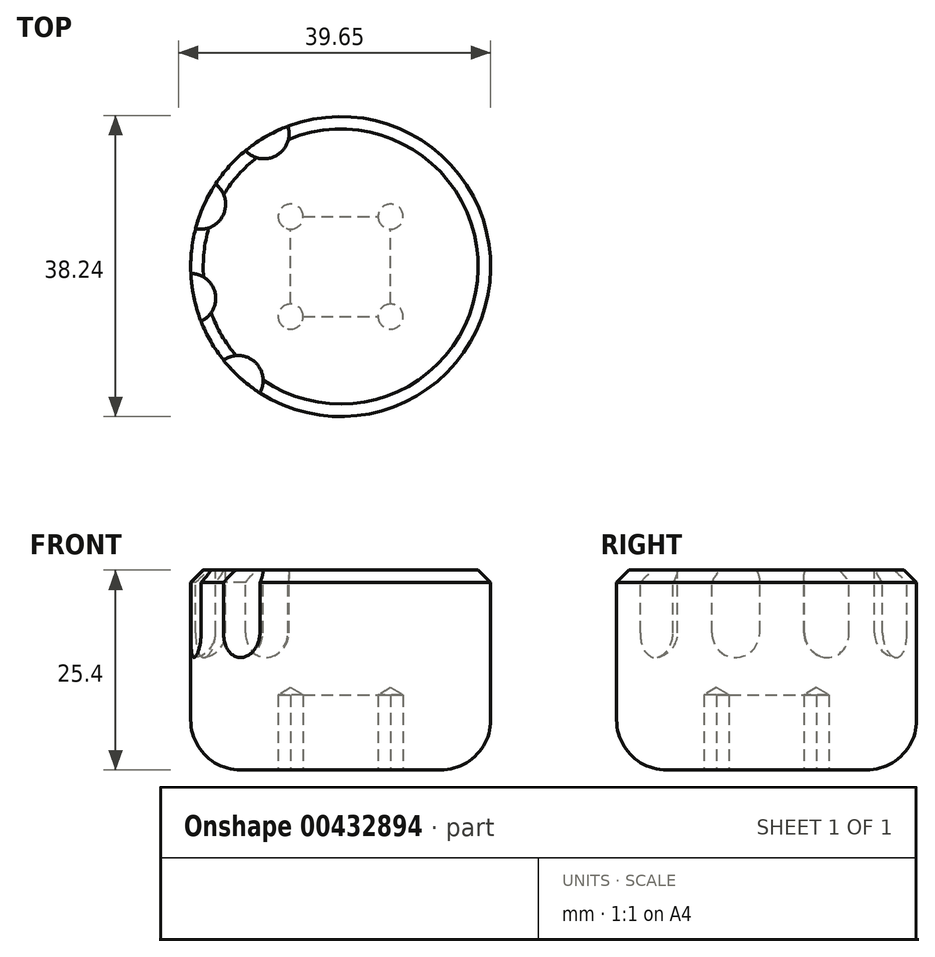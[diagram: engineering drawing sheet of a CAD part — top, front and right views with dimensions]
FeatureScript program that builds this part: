
annotation { "Feature Type Name" : "Feature", "Feature Type Description" : "" }
export const myFeature = defineFeature(function(context is Context, id is Id, definition is map)
    precondition{}
    {
        {
            var Q0;
            Q0=qCreatedBy(makeId("Top.planeOp"),FACE);
            var sketch = newSketch(context, id + "F0", { "sketchPlane" : qUnion([Q0])});
            skCircle(sketch, "E0", {"center": v(0, 0) * mm, "radius": 19.05 * mm});
            skSolve(sketch);
        }
        {
            var Q0;
            Q0 = qSketchRegion(id + "F0", true);
            extrude(context, id + "F1", {"entities" : qUnion([Q0]), "depth" : 25.4 * mm});
        }
        {
            var Q0;
            Q0=makeQuery(id+"F1.opExtrude","CAP_FACE",FACE,{"disambiguationData":[OSD([sQuery(id+"F0.wireOp",EDGE,"E0")])],"isStart":false});
            var sketch = newSketch(context, id + "F2", { "sketchPlane" : qUnion([Q0])});
            skCircle(sketch, "E1.cCircle", {"center": v(0, 0) * mm, "radius": 19.05 * mm, "construction": true});
            skLineSegment(sketch, "E1.0", {"start": v(-19.05, -4.05) * mm, "end": v(-19.05, 4.05) * mm});
            skLineSegment(sketch, "E1.1", {"start": v(-19.05, 4.05) * mm, "end": v(-15.76, 11.45) * mm});
            skLineSegment(sketch, "E1.2", {"start": v(-15.76, 11.45) * mm, "end": v(-9.74, 16.87) * mm});
            skLineSegment(sketch, "E1.3", {"start": v(-9.74, 16.87) * mm, "end": v(-2.04, 19.37) * mm});
            skLineSegment(sketch, "E1.4", {"start": v(-2.04, 19.37) * mm, "end": v(6.02, 18.52) * mm});
            skLineSegment(sketch, "E1.5", {"start": v(6.02, 18.52) * mm, "end": v(13.03, 14.47) * mm});
            skLineSegment(sketch, "E1.6", {"start": v(13.03, 14.47) * mm, "end": v(17.8, 7.92) * mm});
            skLineSegment(sketch, "E1.7", {"start": v(17.8, 7.92) * mm, "end": v(19.48, 0) * mm});
            skLineSegment(sketch, "E1.8", {"start": v(19.48, 0) * mm, "end": v(17.8, -7.92) * mm});
            skLineSegment(sketch, "E1.9", {"start": v(17.8, -7.92) * mm, "end": v(13.03, -14.47) * mm});
            skLineSegment(sketch, "E1.10", {"start": v(13.03, -14.47) * mm, "end": v(6.02, -18.52) * mm});
            skLineSegment(sketch, "E1.11", {"start": v(6.02, -18.52) * mm, "end": v(-2.04, -19.37) * mm});
            skLineSegment(sketch, "E1.12", {"start": v(-2.04, -19.37) * mm, "end": v(-9.74, -16.87) * mm});
            skLineSegment(sketch, "E1.13", {"start": v(-9.74, -16.87) * mm, "end": v(-15.76, -11.45) * mm});
            skLineSegment(sketch, "E1.14", {"start": v(-15.76, -11.45) * mm, "end": v(-19.05, -4.05) * mm});
            skPoint(sketch, "E1.0.midPoint", {"position": v(-19.05, 0) * mm});
            skCircle(sketch, "E2", {"center": v(-19.05, -4.05) * mm, "radius": 3.18 * mm});
            skCircle(sketch, "E3.1.0", {"center": v(-13.03, -14.47) * mm, "radius": 3.18 * mm});
            skCircle(sketch, "E3.2.0", {"center": v(-2.04, -19.37) * mm, "radius": 3.18 * mm});
            skCircle(sketch, "E3.3.0", {"center": v(9.74, -16.87) * mm, "radius": 3.18 * mm});
            skCircle(sketch, "E3.4.0", {"center": v(17.8, -7.92) * mm, "radius": 3.18 * mm});
            skCircle(sketch, "E3.5.0", {"center": v(19.05, 4.05) * mm, "radius": 3.18 * mm});
            skCircle(sketch, "E3.6.0", {"center": v(13.03, 14.47) * mm, "radius": 3.18 * mm});
            skCircle(sketch, "E3.7.0", {"center": v(2.04, 19.37) * mm, "radius": 3.18 * mm});
            skCircle(sketch, "E3.8.0", {"center": v(-9.74, 16.87) * mm, "radius": 3.18 * mm});
            skCircle(sketch, "E3.9.0", {"center": v(-17.8, 7.92) * mm, "radius": 3.18 * mm});
            skSolve(sketch);
        }
        {
            var Q0;
            {var subQ0=sQuery(id+"F2.wireOp",EDGE,"E3.9.0");var subQ1=makeQuery(id+"F1.opExtrude","CAP_EDGE",EDGE,{"disambiguationData":[OSD([sQuery(id+"F0.wireOp",EDGE,"E0")])],"isStart":false});var subQ2=makeQuery(id+"F2.imprint","INTERSECT",VERTEX,{"disambiguationData":[OD(0.0)],"derivedFrom":[subQ1,subQ0]});Q0=makeQuery(id+"F2.imprint","IMPRINT",FACE,{"disambiguationData":[TD([[makeQuery(id+"F2.imprint","IMPRINT",EDGE,{"disambiguationData":[TD([[subQ2,1.0]])],"derivedFrom":subQ0}),1.0]])]});}
            var Q1;
            {var subQ0=sQuery(id+"F2.wireOp",EDGE,"E2");var subQ1=makeQuery(id+"F1.opExtrude","CAP_EDGE",EDGE,{"disambiguationData":[OSD([sQuery(id+"F0.wireOp",EDGE,"E0")])],"isStart":false});var subQ2=makeQuery(id+"F2.imprint","INTERSECT",VERTEX,{"disambiguationData":[OD(0.0)],"derivedFrom":[subQ1,subQ0]});Q1=makeQuery(id+"F2.imprint","IMPRINT",FACE,{"disambiguationData":[TD([[makeQuery(id+"F2.imprint","IMPRINT",EDGE,{"disambiguationData":[TD([[subQ2,1.0]])],"derivedFrom":subQ0}),1.0]])]});}
            var Q2;
            {var subQ0=sQuery(id+"F2.wireOp",EDGE,"E3.1.0");var subQ1=makeQuery(id+"F1.opExtrude","CAP_EDGE",EDGE,{"disambiguationData":[OSD([sQuery(id+"F0.wireOp",EDGE,"E0")])],"isStart":false});var subQ2=makeQuery(id+"F2.imprint","INTERSECT",VERTEX,{"disambiguationData":[OD(0.0)],"derivedFrom":[subQ1,subQ0]});Q2=makeQuery(id+"F2.imprint","IMPRINT",FACE,{"disambiguationData":[TD([[makeQuery(id+"F2.imprint","IMPRINT",EDGE,{"disambiguationData":[TD([[subQ2,1.0]])],"derivedFrom":subQ0}),1.0]])]});}
            var Q3;
            {var subQ0=sQuery(id+"F2.wireOp",EDGE,"E3.2.0");var subQ1=makeQuery(id+"F1.opExtrude","CAP_EDGE",EDGE,{"disambiguationData":[OSD([sQuery(id+"F0.wireOp",EDGE,"E0")])],"isStart":false});var subQ2=makeQuery(id+"F2.imprint","INTERSECT",VERTEX,{"disambiguationData":[OD(0.0)],"derivedFrom":[subQ1,subQ0]});Q3=makeQuery(id+"F2.imprint","IMPRINT",FACE,{"disambiguationData":[TD([[makeQuery(id+"F2.imprint","IMPRINT",EDGE,{"disambiguationData":[TD([[subQ2,1.0]])],"derivedFrom":subQ0}),1.0]])]});}
            var Q4;
            {var subQ0=sQuery(id+"F2.wireOp",EDGE,"E3.3.0");var subQ1=makeQuery(id+"F1.opExtrude","CAP_EDGE",EDGE,{"disambiguationData":[OSD([sQuery(id+"F0.wireOp",EDGE,"E0")])],"isStart":false});var subQ2=makeQuery(id+"F2.imprint","INTERSECT",VERTEX,{"disambiguationData":[OD(0.0)],"derivedFrom":[subQ1,subQ0]});Q4=makeQuery(id+"F2.imprint","IMPRINT",FACE,{"disambiguationData":[TD([[makeQuery(id+"F2.imprint","IMPRINT",EDGE,{"disambiguationData":[TD([[subQ2,1.0]])],"derivedFrom":subQ0}),1.0]])]});}
            var Q5;
            {var subQ0=sQuery(id+"F2.wireOp",EDGE,"E3.4.0");var subQ1=makeQuery(id+"F1.opExtrude","CAP_EDGE",EDGE,{"disambiguationData":[OSD([sQuery(id+"F0.wireOp",EDGE,"E0")])],"isStart":false});var subQ2=makeQuery(id+"F2.imprint","INTERSECT",VERTEX,{"disambiguationData":[OD(0.0)],"derivedFrom":[subQ1,subQ0]});Q5=makeQuery(id+"F2.imprint","IMPRINT",FACE,{"disambiguationData":[TD([[makeQuery(id+"F2.imprint","IMPRINT",EDGE,{"disambiguationData":[TD([[subQ2,1.0]])],"derivedFrom":subQ0}),1.0]])]});}
            var Q6;
            {var subQ0=sQuery(id+"F2.wireOp",EDGE,"E3.5.0");var subQ1=makeQuery(id+"F1.opExtrude","CAP_EDGE",EDGE,{"disambiguationData":[OSD([sQuery(id+"F0.wireOp",EDGE,"E0")])],"isStart":false});var subQ2=makeQuery(id+"F2.imprint","INTERSECT",VERTEX,{"disambiguationData":[OD(0.0)],"derivedFrom":[subQ1,subQ0]});Q6=makeQuery(id+"F2.imprint","IMPRINT",FACE,{"disambiguationData":[TD([[makeQuery(id+"F2.imprint","IMPRINT",EDGE,{"disambiguationData":[TD([[subQ2,1.0]])],"derivedFrom":subQ0}),1.0]])]});}
            var Q7;
            {var subQ0=sQuery(id+"F2.wireOp",EDGE,"E3.6.0");var subQ1=makeQuery(id+"F1.opExtrude","CAP_EDGE",EDGE,{"disambiguationData":[OSD([sQuery(id+"F0.wireOp",EDGE,"E0")])],"isStart":false});var subQ2=makeQuery(id+"F2.imprint","INTERSECT",VERTEX,{"disambiguationData":[OD(0.0)],"derivedFrom":[subQ1,subQ0]});Q7=makeQuery(id+"F2.imprint","IMPRINT",FACE,{"disambiguationData":[TD([[makeQuery(id+"F2.imprint","IMPRINT",EDGE,{"disambiguationData":[TD([[subQ2,1.0]])],"derivedFrom":subQ0}),1.0]])]});}
            var Q8;
            {var subQ0=sQuery(id+"F2.wireOp",EDGE,"E3.7.0");var subQ1=makeQuery(id+"F1.opExtrude","CAP_EDGE",EDGE,{"disambiguationData":[OSD([sQuery(id+"F0.wireOp",EDGE,"E0")])],"isStart":false});var subQ2=makeQuery(id+"F2.imprint","INTERSECT",VERTEX,{"disambiguationData":[OD(0.0)],"derivedFrom":[subQ1,subQ0]});Q8=makeQuery(id+"F2.imprint","IMPRINT",FACE,{"disambiguationData":[TD([[makeQuery(id+"F2.imprint","IMPRINT",EDGE,{"disambiguationData":[TD([[subQ2,1.0]])],"derivedFrom":subQ0}),1.0]])]});}
            var Q9;
            {var subQ0=sQuery(id+"F2.wireOp",EDGE,"E3.8.0");var subQ1=makeQuery(id+"F1.opExtrude","CAP_EDGE",EDGE,{"disambiguationData":[OSD([sQuery(id+"F0.wireOp",EDGE,"E0")])],"isStart":false});var subQ2=makeQuery(id+"F2.imprint","INTERSECT",VERTEX,{"disambiguationData":[OD(0.0)],"derivedFrom":[subQ1,subQ0]});Q9=makeQuery(id+"F2.imprint","IMPRINT",FACE,{"disambiguationData":[TD([[makeQuery(id+"F2.imprint","IMPRINT",EDGE,{"disambiguationData":[TD([[subQ2,1.0]])],"derivedFrom":subQ0}),1.0]])]});}
            extrude(context, id + "F3", {"entities" : qUnion([Q0, Q1, Q2, Q3, Q4, Q5, Q6, Q7, Q8, Q9]), "operationType" : NewBodyOperationType.REMOVE, "oppositeDirection" : true, "depth" : 11.1 * mm});
        }
        {
            var Q0;
            Q0=makeQuery(id+"F3.boolean.opBoolean","COPY",EDGE,{"derivedFrom":makeQuery(id+"F3.opExtrude","CAP_EDGE",EDGE,{"disambiguationData":[OSD([sQuery(id+"F2.wireOp",EDGE,"E3.7.0")])],"isStart":false})});
            var Q1;
            Q1=makeQuery(id+"F3.boolean.opBoolean","COPY",EDGE,{"derivedFrom":makeQuery(id+"F3.opExtrude","CAP_EDGE",EDGE,{"disambiguationData":[OSD([sQuery(id+"F2.wireOp",EDGE,"E3.6.0")])],"isStart":false})});
            var Q2;
            Q2=makeQuery(id+"F3.boolean.opBoolean","COPY",EDGE,{"derivedFrom":makeQuery(id+"F3.opExtrude","CAP_EDGE",EDGE,{"disambiguationData":[OSD([sQuery(id+"F2.wireOp",EDGE,"E3.5.0")])],"isStart":false})});
            var Q3;
            Q3=makeQuery(id+"F3.boolean.opBoolean","COPY",EDGE,{"derivedFrom":makeQuery(id+"F3.opExtrude","CAP_EDGE",EDGE,{"disambiguationData":[OSD([sQuery(id+"F2.wireOp",EDGE,"E3.4.0")])],"isStart":false})});
            var Q4;
            Q4=makeQuery(id+"F3.boolean.opBoolean","COPY",EDGE,{"derivedFrom":makeQuery(id+"F3.opExtrude","CAP_EDGE",EDGE,{"disambiguationData":[OSD([sQuery(id+"F2.wireOp",EDGE,"E3.3.0")])],"isStart":false})});
            var Q5;
            Q5=makeQuery(id+"F3.boolean.opBoolean","COPY",EDGE,{"derivedFrom":makeQuery(id+"F3.opExtrude","CAP_EDGE",EDGE,{"disambiguationData":[OSD([sQuery(id+"F2.wireOp",EDGE,"E3.2.0")])],"isStart":false})});
            var Q6;
            Q6=makeQuery(id+"F3.boolean.opBoolean","COPY",EDGE,{"derivedFrom":makeQuery(id+"F3.opExtrude","CAP_EDGE",EDGE,{"disambiguationData":[OSD([sQuery(id+"F2.wireOp",EDGE,"E3.1.0")])],"isStart":false})});
            var Q7;
            Q7=makeQuery(id+"F3.boolean.opBoolean","COPY",EDGE,{"derivedFrom":makeQuery(id+"F3.opExtrude","CAP_EDGE",EDGE,{"disambiguationData":[OSD([sQuery(id+"F2.wireOp",EDGE,"E2")])],"isStart":false})});
            var Q8;
            Q8=makeQuery(id+"F3.boolean.opBoolean","COPY",EDGE,{"derivedFrom":makeQuery(id+"F3.opExtrude","CAP_EDGE",EDGE,{"disambiguationData":[OSD([sQuery(id+"F2.wireOp",EDGE,"E3.9.0")])],"isStart":false})});
            var Q9;
            Q9=makeQuery(id+"F3.boolean.opBoolean","COPY",EDGE,{"derivedFrom":makeQuery(id+"F3.opExtrude","CAP_EDGE",EDGE,{"disambiguationData":[OSD([sQuery(id+"F2.wireOp",EDGE,"E3.8.0")])],"isStart":false})});
            fillet(context, id + "F4", {"entities" : qUnion([Q0, Q1, Q2, Q3, Q4, Q5, Q6, Q7, Q8, Q9]), "radius" : 3.17 * mm, "allowEdgeOverflow" : false});
        }
        {
            var Q0;
            {var subQ0=sQuery(id+"F0.wireOp",EDGE,"E0");Q0=makeQuery(id+"F3.boolean.opBoolean","SPLIT",EDGE,{"disambiguationData":[TD([makeQuery(id+"F1.opExtrude","SWEPT_FACE",FACE,{"disambiguationData":[OSD([subQ0])]}),makeQuery(id+"F1.opExtrude","CAP_FACE",FACE,{"disambiguationData":[OSD([subQ0])],"isStart":false}),makeQuery(id+"F3.opExtrude","SWEPT_FACE",FACE,{"disambiguationData":[OSD([sQuery(id+"F2.wireOp",EDGE,"E3.5.0")])]}),makeQuery(id+"F3.opExtrude","SWEPT_FACE",FACE,{"disambiguationData":[OSD([sQuery(id+"F2.wireOp",EDGE,"E3.6.0")])]})])],"derivedFrom":makeQuery(id+"F1.opExtrude","CAP_EDGE",EDGE,{"disambiguationData":[OSD([subQ0])],"isStart":false})});}
            var Q1;
            {var subQ0=sQuery(id+"F0.wireOp",EDGE,"E0");Q1=makeQuery(id+"F3.boolean.opBoolean","SPLIT",EDGE,{"disambiguationData":[TD([makeQuery(id+"F1.opExtrude","SWEPT_FACE",FACE,{"disambiguationData":[OSD([subQ0])]}),makeQuery(id+"F1.opExtrude","CAP_FACE",FACE,{"disambiguationData":[OSD([subQ0])],"isStart":false}),makeQuery(id+"F3.opExtrude","SWEPT_FACE",FACE,{"disambiguationData":[OSD([sQuery(id+"F2.wireOp",EDGE,"E3.4.0")])]}),makeQuery(id+"F3.opExtrude","SWEPT_FACE",FACE,{"disambiguationData":[OSD([sQuery(id+"F2.wireOp",EDGE,"E3.5.0")])]})])],"derivedFrom":makeQuery(id+"F1.opExtrude","CAP_EDGE",EDGE,{"disambiguationData":[OSD([subQ0])],"isStart":false})});}
            var Q2;
            {var subQ0=sQuery(id+"F0.wireOp",EDGE,"E0");Q2=makeQuery(id+"F3.boolean.opBoolean","SPLIT",EDGE,{"disambiguationData":[TD([makeQuery(id+"F1.opExtrude","SWEPT_FACE",FACE,{"disambiguationData":[OSD([subQ0])]}),makeQuery(id+"F1.opExtrude","CAP_FACE",FACE,{"disambiguationData":[OSD([subQ0])],"isStart":false}),makeQuery(id+"F3.opExtrude","SWEPT_FACE",FACE,{"disambiguationData":[OSD([sQuery(id+"F2.wireOp",EDGE,"E3.3.0")])]}),makeQuery(id+"F3.opExtrude","SWEPT_FACE",FACE,{"disambiguationData":[OSD([sQuery(id+"F2.wireOp",EDGE,"E3.4.0")])]})])],"derivedFrom":makeQuery(id+"F1.opExtrude","CAP_EDGE",EDGE,{"disambiguationData":[OSD([subQ0])],"isStart":false})});}
            var Q3;
            {var subQ0=sQuery(id+"F0.wireOp",EDGE,"E0");Q3=makeQuery(id+"F3.boolean.opBoolean","SPLIT",EDGE,{"disambiguationData":[TD([makeQuery(id+"F1.opExtrude","SWEPT_FACE",FACE,{"disambiguationData":[OSD([subQ0])]}),makeQuery(id+"F1.opExtrude","CAP_FACE",FACE,{"disambiguationData":[OSD([subQ0])],"isStart":false}),makeQuery(id+"F3.opExtrude","SWEPT_FACE",FACE,{"disambiguationData":[OSD([sQuery(id+"F2.wireOp",EDGE,"E3.2.0")])]}),makeQuery(id+"F3.opExtrude","SWEPT_FACE",FACE,{"disambiguationData":[OSD([sQuery(id+"F2.wireOp",EDGE,"E3.3.0")])]})])],"derivedFrom":makeQuery(id+"F1.opExtrude","CAP_EDGE",EDGE,{"disambiguationData":[OSD([subQ0])],"isStart":false})});}
            var Q4;
            {var subQ0=sQuery(id+"F0.wireOp",EDGE,"E0");Q4=makeQuery(id+"F3.boolean.opBoolean","SPLIT",EDGE,{"disambiguationData":[TD([makeQuery(id+"F1.opExtrude","SWEPT_FACE",FACE,{"disambiguationData":[OSD([subQ0])]}),makeQuery(id+"F1.opExtrude","CAP_FACE",FACE,{"disambiguationData":[OSD([subQ0])],"isStart":false}),makeQuery(id+"F3.opExtrude","SWEPT_FACE",FACE,{"disambiguationData":[OSD([sQuery(id+"F2.wireOp",EDGE,"E3.1.0")])]}),makeQuery(id+"F3.opExtrude","SWEPT_FACE",FACE,{"disambiguationData":[OSD([sQuery(id+"F2.wireOp",EDGE,"E3.2.0")])]})])],"derivedFrom":makeQuery(id+"F1.opExtrude","CAP_EDGE",EDGE,{"disambiguationData":[OSD([subQ0])],"isStart":false})});}
            var Q5;
            {var subQ0=sQuery(id+"F0.wireOp",EDGE,"E0");Q5=makeQuery(id+"F3.boolean.opBoolean","SPLIT",EDGE,{"disambiguationData":[TD([makeQuery(id+"F1.opExtrude","SWEPT_FACE",FACE,{"disambiguationData":[OSD([subQ0])]}),makeQuery(id+"F1.opExtrude","CAP_FACE",FACE,{"disambiguationData":[OSD([subQ0])],"isStart":false}),makeQuery(id+"F3.opExtrude","SWEPT_FACE",FACE,{"disambiguationData":[OSD([sQuery(id+"F2.wireOp",EDGE,"E2")])]}),makeQuery(id+"F3.opExtrude","SWEPT_FACE",FACE,{"disambiguationData":[OSD([sQuery(id+"F2.wireOp",EDGE,"E3.1.0")])]})])],"derivedFrom":makeQuery(id+"F1.opExtrude","CAP_EDGE",EDGE,{"disambiguationData":[OSD([subQ0])],"isStart":false})});}
            var Q6;
            {var subQ0=sQuery(id+"F0.wireOp",EDGE,"E0");Q6=makeQuery(id+"F3.boolean.opBoolean","SPLIT",EDGE,{"disambiguationData":[TD([makeQuery(id+"F1.opExtrude","SWEPT_FACE",FACE,{"disambiguationData":[OSD([subQ0])]}),makeQuery(id+"F1.opExtrude","CAP_FACE",FACE,{"disambiguationData":[OSD([subQ0])],"isStart":false}),makeQuery(id+"F3.opExtrude","SWEPT_FACE",FACE,{"disambiguationData":[OSD([sQuery(id+"F2.wireOp",EDGE,"E2")])]}),makeQuery(id+"F3.opExtrude","SWEPT_FACE",FACE,{"disambiguationData":[OSD([sQuery(id+"F2.wireOp",EDGE,"E3.9.0")])]})])],"derivedFrom":makeQuery(id+"F1.opExtrude","CAP_EDGE",EDGE,{"disambiguationData":[OSD([subQ0])],"isStart":false})});}
            var Q7;
            {var subQ0=sQuery(id+"F0.wireOp",EDGE,"E0");Q7=makeQuery(id+"F3.boolean.opBoolean","SPLIT",EDGE,{"disambiguationData":[TD([makeQuery(id+"F1.opExtrude","SWEPT_FACE",FACE,{"disambiguationData":[OSD([subQ0])]}),makeQuery(id+"F1.opExtrude","CAP_FACE",FACE,{"disambiguationData":[OSD([subQ0])],"isStart":false}),makeQuery(id+"F3.opExtrude","SWEPT_FACE",FACE,{"disambiguationData":[OSD([sQuery(id+"F2.wireOp",EDGE,"E3.8.0")])]}),makeQuery(id+"F3.opExtrude","SWEPT_FACE",FACE,{"disambiguationData":[OSD([sQuery(id+"F2.wireOp",EDGE,"E3.9.0")])]})])],"derivedFrom":makeQuery(id+"F1.opExtrude","CAP_EDGE",EDGE,{"disambiguationData":[OSD([subQ0])],"isStart":false})});}
            var Q8;
            {var subQ0=sQuery(id+"F0.wireOp",EDGE,"E0");Q8=makeQuery(id+"F3.boolean.opBoolean","SPLIT",EDGE,{"disambiguationData":[TD([makeQuery(id+"F1.opExtrude","SWEPT_FACE",FACE,{"disambiguationData":[OSD([subQ0])]}),makeQuery(id+"F1.opExtrude","CAP_FACE",FACE,{"disambiguationData":[OSD([subQ0])],"isStart":false}),makeQuery(id+"F3.opExtrude","SWEPT_FACE",FACE,{"disambiguationData":[OSD([sQuery(id+"F2.wireOp",EDGE,"E3.7.0")])]}),makeQuery(id+"F3.opExtrude","SWEPT_FACE",FACE,{"disambiguationData":[OSD([sQuery(id+"F2.wireOp",EDGE,"E3.8.0")])]})])],"derivedFrom":makeQuery(id+"F1.opExtrude","CAP_EDGE",EDGE,{"disambiguationData":[OSD([subQ0])],"isStart":false})});}
            var Q9;
            {var subQ0=sQuery(id+"F0.wireOp",EDGE,"E0");Q9=makeQuery(id+"F3.boolean.opBoolean","SPLIT",EDGE,{"disambiguationData":[TD([makeQuery(id+"F1.opExtrude","SWEPT_FACE",FACE,{"disambiguationData":[OSD([subQ0])]}),makeQuery(id+"F1.opExtrude","CAP_FACE",FACE,{"disambiguationData":[OSD([subQ0])],"isStart":false}),makeQuery(id+"F3.opExtrude","SWEPT_FACE",FACE,{"disambiguationData":[OSD([sQuery(id+"F2.wireOp",EDGE,"E3.6.0")])]}),makeQuery(id+"F3.opExtrude","SWEPT_FACE",FACE,{"disambiguationData":[OSD([sQuery(id+"F2.wireOp",EDGE,"E3.7.0")])]})])],"derivedFrom":makeQuery(id+"F1.opExtrude","CAP_EDGE",EDGE,{"disambiguationData":[OSD([subQ0])],"isStart":false})});}
            chamfer(context, id + "F5", {"entities" : qUnion([Q0, Q1, Q2, Q3, Q4, Q5, Q6, Q7, Q8, Q9]), "width" : 1.59 * mm, "tangentPropagation" : true});
        }
        {
            var Q0;
            Q0=makeQuery(id+"F1.opExtrude","CAP_EDGE",EDGE,{"disambiguationData":[OSD([sQuery(id+"F0.wireOp",EDGE,"E0")])],"isStart":true});
            fillet(context, id + "F6", {"entities" : qUnion([Q0]), "radius" : 6.35 * mm, "tangentPropagation" : true, "allowEdgeOverflow" : false});
        }
        {
            var Q0;
            Q0=makeQuery(id+"F1.opExtrude","CAP_FACE",FACE,{"disambiguationData":[OSD([sQuery(id+"F0.wireOp",EDGE,"E0")])],"isStart":true});
            var sketch = newSketch(context, id + "F7", { "sketchPlane" : qUnion([Q0])});
            skLineSegment(sketch, "E4.bottom", {"start": v(-6.35, 6.35) * mm, "end": v(6.35, 6.35) * mm});
            skLineSegment(sketch, "E4.top", {"start": v(-6.35, -6.35) * mm, "end": v(6.35, -6.35) * mm});
            skLineSegment(sketch, "E4.left", {"start": v(-6.35, 6.35) * mm, "end": v(-6.35, -6.35) * mm});
            skLineSegment(sketch, "E4.right", {"start": v(6.35, 6.35) * mm, "end": v(6.35, -6.35) * mm});
            skPoint(sketch, "E4.middle", {"position": v(0, 0) * mm});
            skSolve(sketch);
        }
        {
            var Q0;
            Q0=sQuery(id+"F7.wireOp",VERTEX,"E4.left.end");
            var Q1;
            Q1=sQuery(id+"F7.wireOp",VERTEX,"E4.bottom.start");
            var Q2;
            Q2=sQuery(id+"F7.wireOp",VERTEX,"E4.bottom.end");
            var Q3;
            Q3=sQuery(id+"F7.wireOp",VERTEX,"E4.right.end");
            var Q4;
            Q4=makeQuery(id+"F1.opExtrude","SWEPT_BODY",BODY,{"disambiguationData":[OSD([sQuery(id+"F0.wireOp",EDGE,"E0")])]});
            hole(context, id + "F8", {"style" : HoleStyle.SIMPLE, "endStyle" : HoleEndStyle.BLIND, "holeDiameter" : 3.17 * mm, "holeDepth" : 9.52 * mm, "isTappedThrough" : true, "tappedDepth" : 12.7 * mm, "tapClearance" : 3, "locations" : qUnion([Q0, Q1, Q2, Q3]), "scope" : qUnion([Q4])});
        }
        {
            var Q0;
            Q0=makeQuery(id+"F7.imprint","IMPRINT",FACE,{"disambiguationData":[TD([[makeQuery(id+"F7.imprint","IMPRINT",EDGE,{"derivedFrom":sQuery(id+"F7.wireOp",EDGE,"E4.bottom")}),-1.0]])]});
            extrude(context, id + "F9", {"entities" : qUnion([Q0]), "operationType" : NewBodyOperationType.REMOVE, "oppositeDirection" : true, "depth" : 9.52 * mm});
        }
    });
